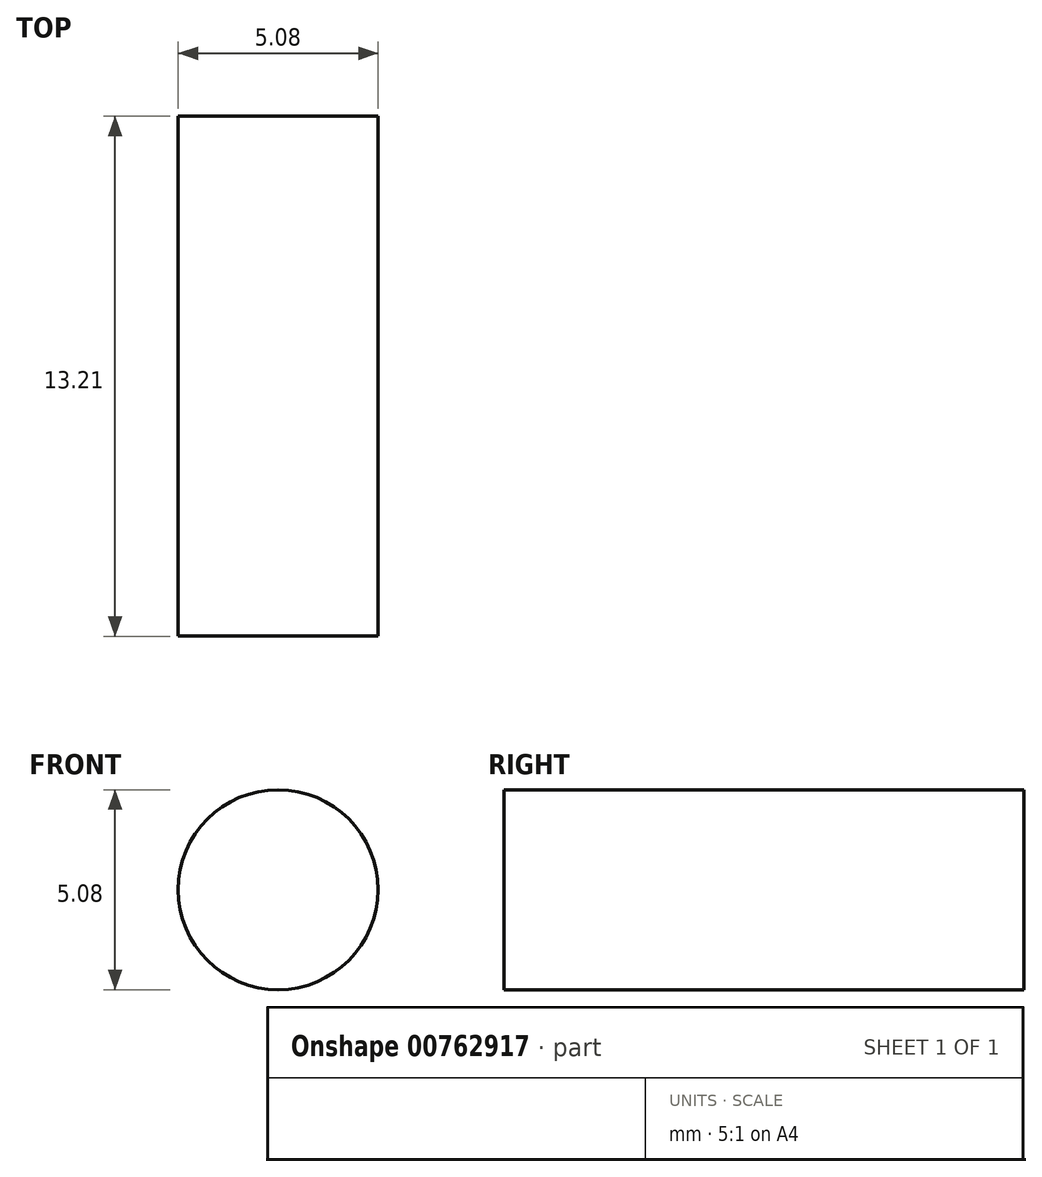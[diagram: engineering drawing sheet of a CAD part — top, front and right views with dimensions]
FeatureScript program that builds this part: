
annotation { "Feature Type Name" : "Feature", "Feature Type Description" : "" }
export const myFeature = defineFeature(function(context is Context, id is Id, definition is map)
    precondition{}
    {
        {
            var Q0;
            Q0=qCreatedBy(makeId("Front.planeOp"),FACE);
            var sketch = newSketch(context, id + "F0", { "sketchPlane" : qUnion([Q0])});
            skCircle(sketch, "E0", {"center": v(0, 0) * mm, "radius": 2.54 * mm});
            skSolve(sketch);
        }
        {
            var Q0;
            Q0=makeQuery(id+"F0.imprint","IMPRINT",FACE,{"disambiguationData":[TD([[makeQuery(id+"F0.imprint","IMPRINT",EDGE,{"derivedFrom":sQuery(id+"F0.wireOp",EDGE,"E0")}),1.0]])]});
            extrude(context, id + "F1", {"entities" : qUnion([Q0]), "depth" : 13.2 * mm, "offsetDistance" : 25.4 * mm});
        }
    });
